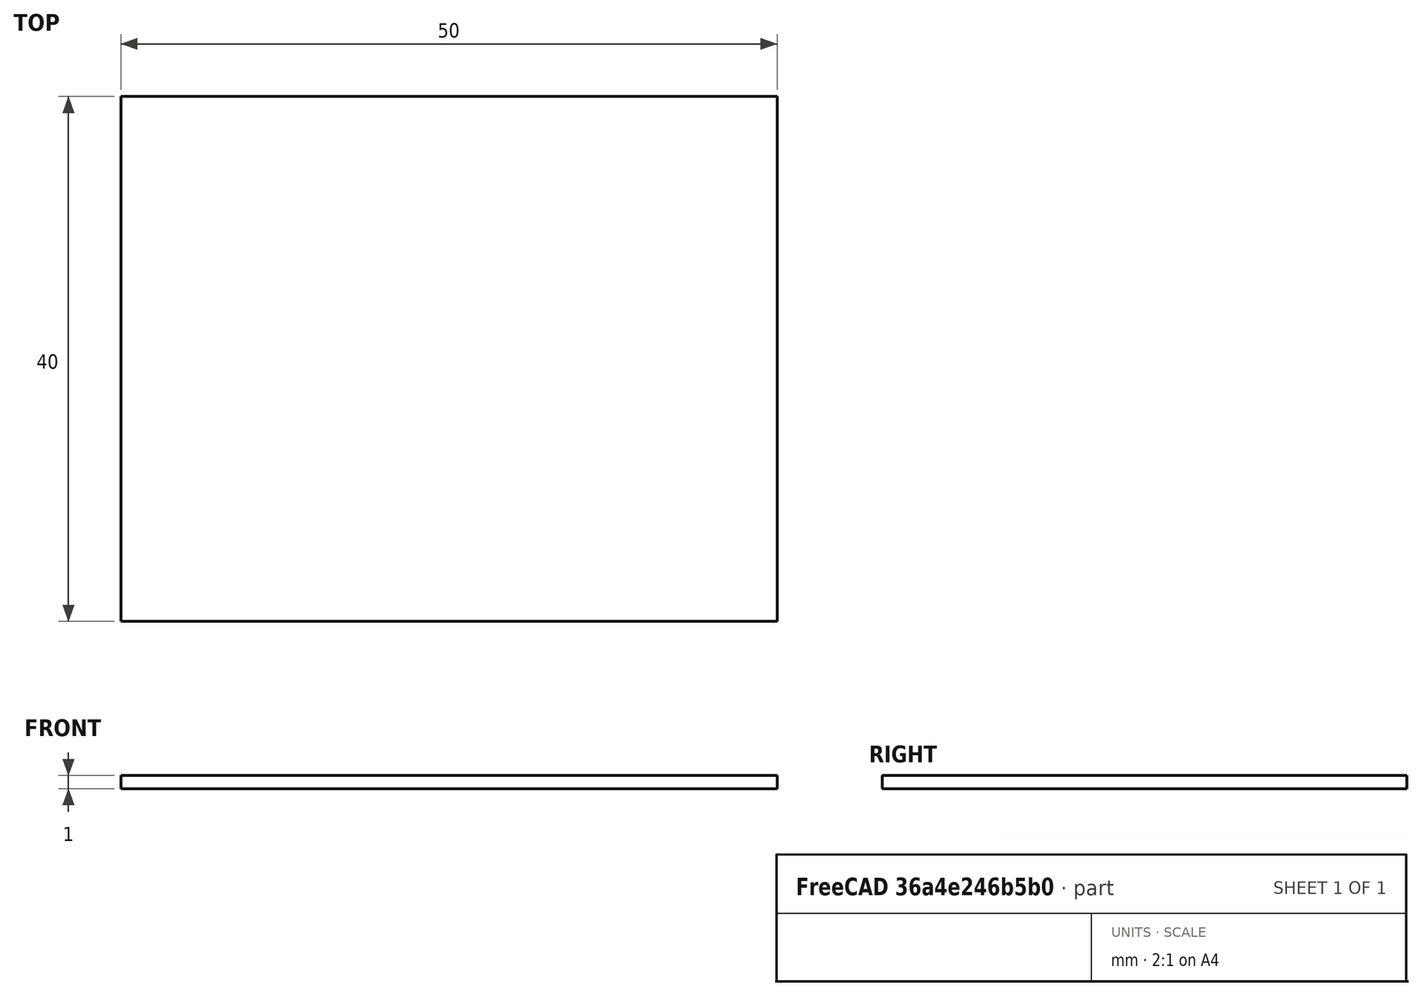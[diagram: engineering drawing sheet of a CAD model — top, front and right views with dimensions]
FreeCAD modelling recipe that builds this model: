
FCSTD DOCUMENT  (FreeCAD 2023.1231R38924 (Git))
Label: sidebracket
License: All rights reserved
objects: Sketcher::SketchObject×1, PartDesign::Pad×1, PartDesign::Body×1
note: 6 computed .brp shape members not serialized (recipe doc carries the construction recipe); baked Part::Feature solids carry a one-line shape summary decoded from their .brp

FEATURE [Sketcher::SketchObject] Sketch
  ArcFitTolerance = 1e-06
  ExternalBSplineMaxDegree = 5
  ExternalBSplineTolerance = 0.0001
  FullyConstrained = true
  InternalTolerance = 1e-06
  InvalidShape = false
  MakeInternals = false
  TreeRank = 11
  ValidateShape = false
  sketch-geometry (4):
    g0: LineSegment StartX=50 StartY=0 StartZ=0 EndX=0 EndY=0 EndZ=0
    g1: LineSegment StartX=0 StartY=0 StartZ=0 EndX=0 EndY=40 EndZ=0
    g2: LineSegment StartX=0 StartY=40 StartZ=0 EndX=50 EndY=40 EndZ=0
    g3: LineSegment StartX=50 StartY=40 StartZ=0 EndX=50 EndY=0 EndZ=0
  constraints (12):
    c: Coincident(g0,g1)
    c: Coincident(g1,g2)
    c: Coincident(g2,g3)
    c: Coincident(g3,g0)
    c: Horizontal(g0)
    c: Horizontal(g2)
    c: Vertical(g1)
    c: Vertical(g3)
    c: Distance(g2) = 50
    c: Distance(g3) = 40
    c: DistanceY(g0,g-1) = 0
    c: DistanceX(g0,g-1) = 0
FEATURE [PartDesign::Pad] Pad
  AddSubType = 0
  AlongSketchNormal = false
  AutoTaperInnerAngle = true
  CheckUpToFaceLimits = true
  ClaimChildren = false
  Direction = (0,0,1)
  Fit = 0
  FitJoin = 0
  InnerFit = 0
  InnerFitJoin = 0
  InvalidShape = false
  Length = 1
  Length2 = 10
  Linearize = true
  NewSolid = false
  Profile = -> Sketch
  ReferenceAxis = -> Sketch [N_Axis]
  Suppress = false
  TaperInnerAngle = 0
  TaperInnerAngleRev = 0
  TreeRank = 12
  Type = 0
  ValidateShape = false
  _ProfileBasedVersion = 1
FEATURE [PartDesign::Body] Body
  AutoGroupSolids = false
  ClaimAllChildren = false
  ExportMode = 0
  Group = -> [Sketch,Pad]
  InvalidShape = false
  Origin = -> Origin
  Tip = -> Pad
  TreeRank = 10
  ValidateShape = false
  _ExportChildren = -> [Pad]
  _GroupVersion = 1
